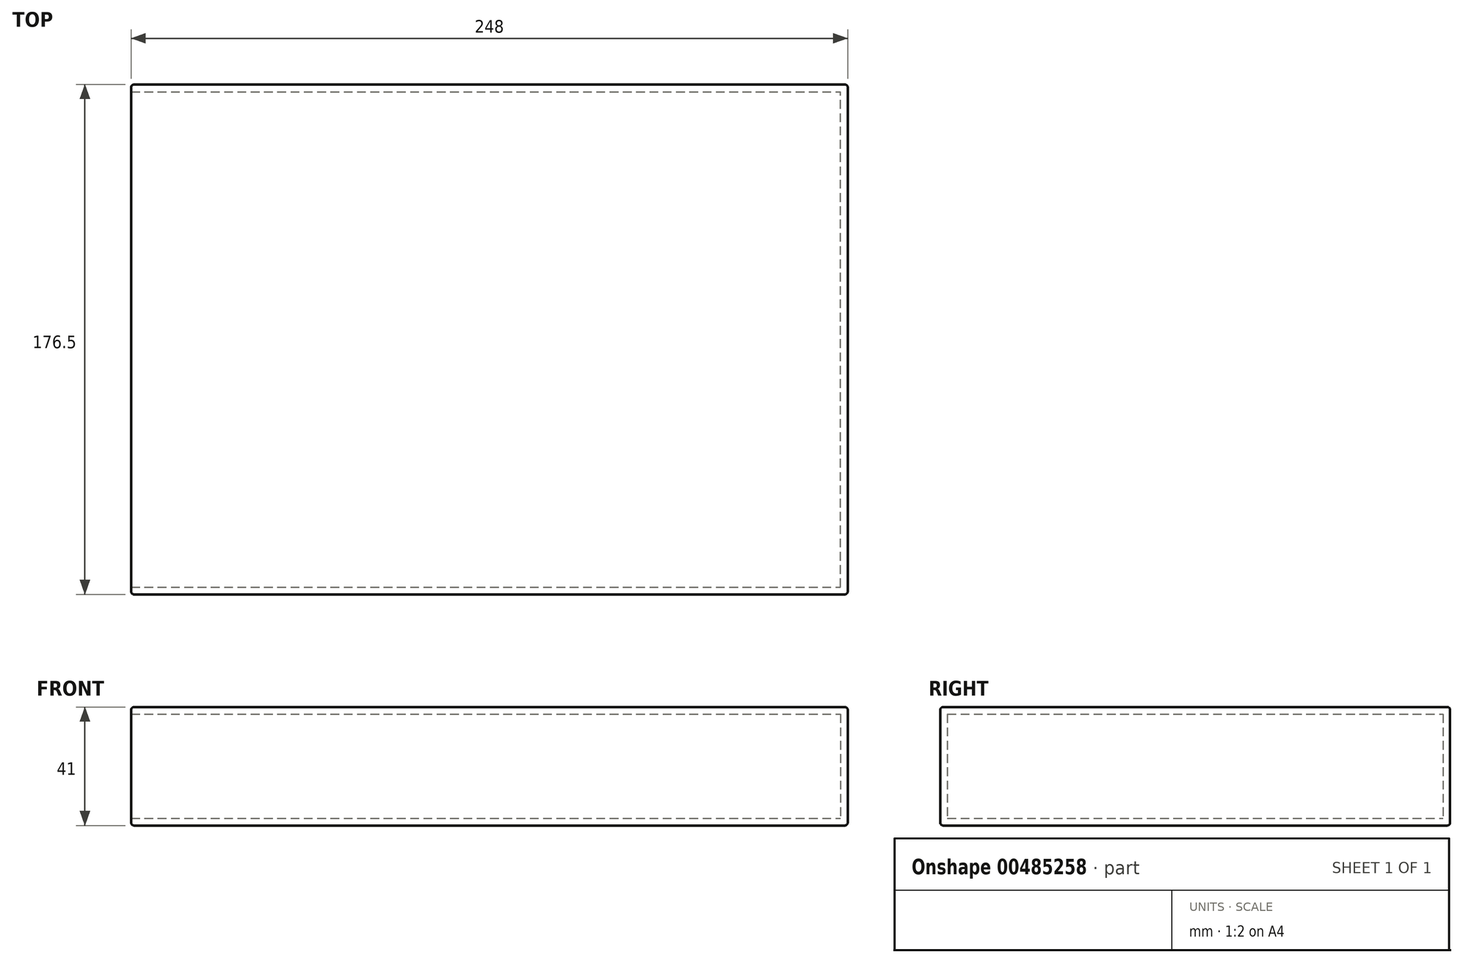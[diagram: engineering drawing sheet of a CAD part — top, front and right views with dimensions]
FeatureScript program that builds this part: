
annotation { "Feature Type Name" : "Feature", "Feature Type Description" : "" }
export const myFeature = defineFeature(function(context is Context, id is Id, definition is map)
    precondition{}
    {
        {
            var Q0;
            Q0=qCreatedBy(makeId("Top.planeOp"),FACE);
            var sketch = newSketch(context, id + "F0", { "sketchPlane" : qUnion([Q0])});
            skLineSegment(sketch, "E0.bottom", {"start": v(0, 0) * mm, "end": v(248, 0) * mm});
            skLineSegment(sketch, "E0.top", {"start": v(0, 176.5) * mm, "end": v(248, 176.5) * mm});
            skLineSegment(sketch, "E0.left", {"start": v(0, 0) * mm, "end": v(0, 176.5) * mm});
            skLineSegment(sketch, "E0.right", {"start": v(248, 0) * mm, "end": v(248, 176.5) * mm});
            skSolve(sketch);
        }
        {
            var Q0;
            Q0=makeQuery(id+"F0.imprint","IMPRINT",FACE,{"disambiguationData":[TD([[makeQuery(id+"F0.imprint","IMPRINT",EDGE,{"derivedFrom":sQuery(id+"F0.wireOp",EDGE,"E0.bottom")}),1.0]])]});
            extrude(context, id + "F1", {"entities" : qUnion([Q0]), "depth" : 41 * mm});
        }
        {
            var Q0;
            Q0=makeQuery(id+"F1.opExtrude","SWEPT_FACE",FACE,{"disambiguationData":[OSD([sQuery(id+"F0.wireOp",EDGE,"E0.left")])]});
            var sketch = newSketch(context, id + "F2", { "sketchPlane" : qUnion([Q0])});
            skLineSegment(sketch, "E1.bottom", {"start": v(-174.5, 2) * mm, "end": v(-2, 2) * mm});
            skLineSegment(sketch, "E1.top", {"start": v(-174.5, 39) * mm, "end": v(-2, 39) * mm});
            skLineSegment(sketch, "E1.left", {"start": v(-174.5, 2) * mm, "end": v(-174.5, 39) * mm});
            skLineSegment(sketch, "E1.right", {"start": v(-2, 2) * mm, "end": v(-2, 39) * mm});
            skLineSegment(sketch, "E2.0", {"start": v(0, 41) * mm, "end": v(-176.5, 41) * mm});
            skSolve(sketch);
        }
        {
            var Q0;
            Q0=makeQuery(id+"F1.opExtrude","SWEPT_FACE",FACE,{"disambiguationData":[OSD([sQuery(id+"F0.wireOp",EDGE,"E0.left")])]});
            shell(context, id + "F3", {"entities" : qUnion([Q0]), "thickness" : 2.5 * mm});
        }
        {
            var Q0;
            Q0=makeQuery(id+"F1.opExtrude","CAP_EDGE",EDGE,{"disambiguationData":[OSD([sQuery(id+"F0.wireOp",EDGE,"E0.top")])],"isStart":false});
            var Q1;
            Q1=makeQuery(id+"F1.opExtrude","CAP_EDGE",EDGE,{"disambiguationData":[OSD([sQuery(id+"F0.wireOp",EDGE,"E0.top")])],"isStart":true});
            var Q2;
            Q2=makeQuery(id+"F1.opExtrude","SWEPT_EDGE",EDGE,{"disambiguationData":[OSD([sQuery(id+"F0.wireOp",EDGE,"E0.top"),sQuery(id+"F0.wireOp",EDGE,"E0.left")])]});
            var Q3;
            Q3=makeQuery(id+"FjTRSG0J6b65jRQ_1.boolean.opBoolean","COPY",EDGE,{"derivedFrom":makeQuery(id+"FjTRSG0J6b65jRQ_1.opExtrude","CAP_EDGE",EDGE,{"disambiguationData":[OSD([sQuery(id+"F2.wireOp",EDGE,"E1.top")])],"isStart":true})});
            var Q4;
            Q4=makeQuery(id+"FjTRSG0J6b65jRQ_1.boolean.opBoolean","COPY",EDGE,{"derivedFrom":makeQuery(id+"FjTRSG0J6b65jRQ_1.opExtrude","CAP_EDGE",EDGE,{"disambiguationData":[OSD([sQuery(id+"F2.wireOp",EDGE,"E1.bottom")])],"isStart":true})});
            var Q5;
            Q5=makeQuery(id+"F1.opExtrude","CAP_EDGE",EDGE,{"disambiguationData":[OSD([sQuery(id+"F0.wireOp",EDGE,"E0.left")])],"isStart":true});
            var Q6;
            Q6=makeQuery(id+"F1.opExtrude","CAP_EDGE",EDGE,{"disambiguationData":[OSD([sQuery(id+"F0.wireOp",EDGE,"E0.left")])],"isStart":false});
            var Q7;
            Q7=makeQuery(id+"FjTRSG0J6b65jRQ_1.boolean.opBoolean","COPY",EDGE,{"derivedFrom":makeQuery(id+"FjTRSG0J6b65jRQ_1.opExtrude","CAP_EDGE",EDGE,{"disambiguationData":[OSD([sQuery(id+"F2.wireOp",EDGE,"E1.right")])],"isStart":true})});
            var Q8;
            Q8=makeQuery(id+"F1.opExtrude","CAP_EDGE",EDGE,{"disambiguationData":[OSD([sQuery(id+"F0.wireOp",EDGE,"E0.bottom")])],"isStart":false});
            var Q9;
            Q9=makeQuery(id+"F1.opExtrude","SWEPT_EDGE",EDGE,{"disambiguationData":[OSD([sQuery(id+"F0.wireOp",EDGE,"E0.bottom"),sQuery(id+"F0.wireOp",EDGE,"E0.left")])]});
            var Q10;
            Q10=makeQuery(id+"FjTRSG0J6b65jRQ_1.boolean.opBoolean","COPY",EDGE,{"derivedFrom":makeQuery(id+"FjTRSG0J6b65jRQ_1.opExtrude","CAP_EDGE",EDGE,{"disambiguationData":[OSD([sQuery(id+"F2.wireOp",EDGE,"E1.left")])],"isStart":true})});
            var Q11;
            Q11=makeQuery(id+"F1.opExtrude","CAP_EDGE",EDGE,{"disambiguationData":[OSD([sQuery(id+"F0.wireOp",EDGE,"E0.bottom")])],"isStart":true});
            var Q12;
            Q12=makeQuery(id+"F1.opExtrude","SWEPT_EDGE",EDGE,{"disambiguationData":[OSD([sQuery(id+"F0.wireOp",EDGE,"E0.bottom"),sQuery(id+"F0.wireOp",EDGE,"E0.right")])]});
            var Q13;
            Q13=makeQuery(id+"F1.opExtrude","CAP_EDGE",EDGE,{"disambiguationData":[OSD([sQuery(id+"F0.wireOp",EDGE,"E0.right")])],"isStart":false});
            var Q14;
            Q14=makeQuery(id+"F1.opExtrude","CAP_EDGE",EDGE,{"disambiguationData":[OSD([sQuery(id+"F0.wireOp",EDGE,"E0.right")])],"isStart":true});
            var Q15;
            Q15=makeQuery(id+"F1.opExtrude","SWEPT_EDGE",EDGE,{"disambiguationData":[OSD([sQuery(id+"F0.wireOp",EDGE,"E0.top"),sQuery(id+"F0.wireOp",EDGE,"E0.right")])]});
            fillet(context, id + "F4", {"entities" : qUnion([Q0, Q1, Q2, Q3, Q4, Q5, Q6, Q7, Q8, Q9, Q10, Q11, Q12, Q13, Q14, Q15]), "radius" : 1 * mm, "tangentPropagation" : true, "allowEdgeOverflow" : false});
        }
    });
